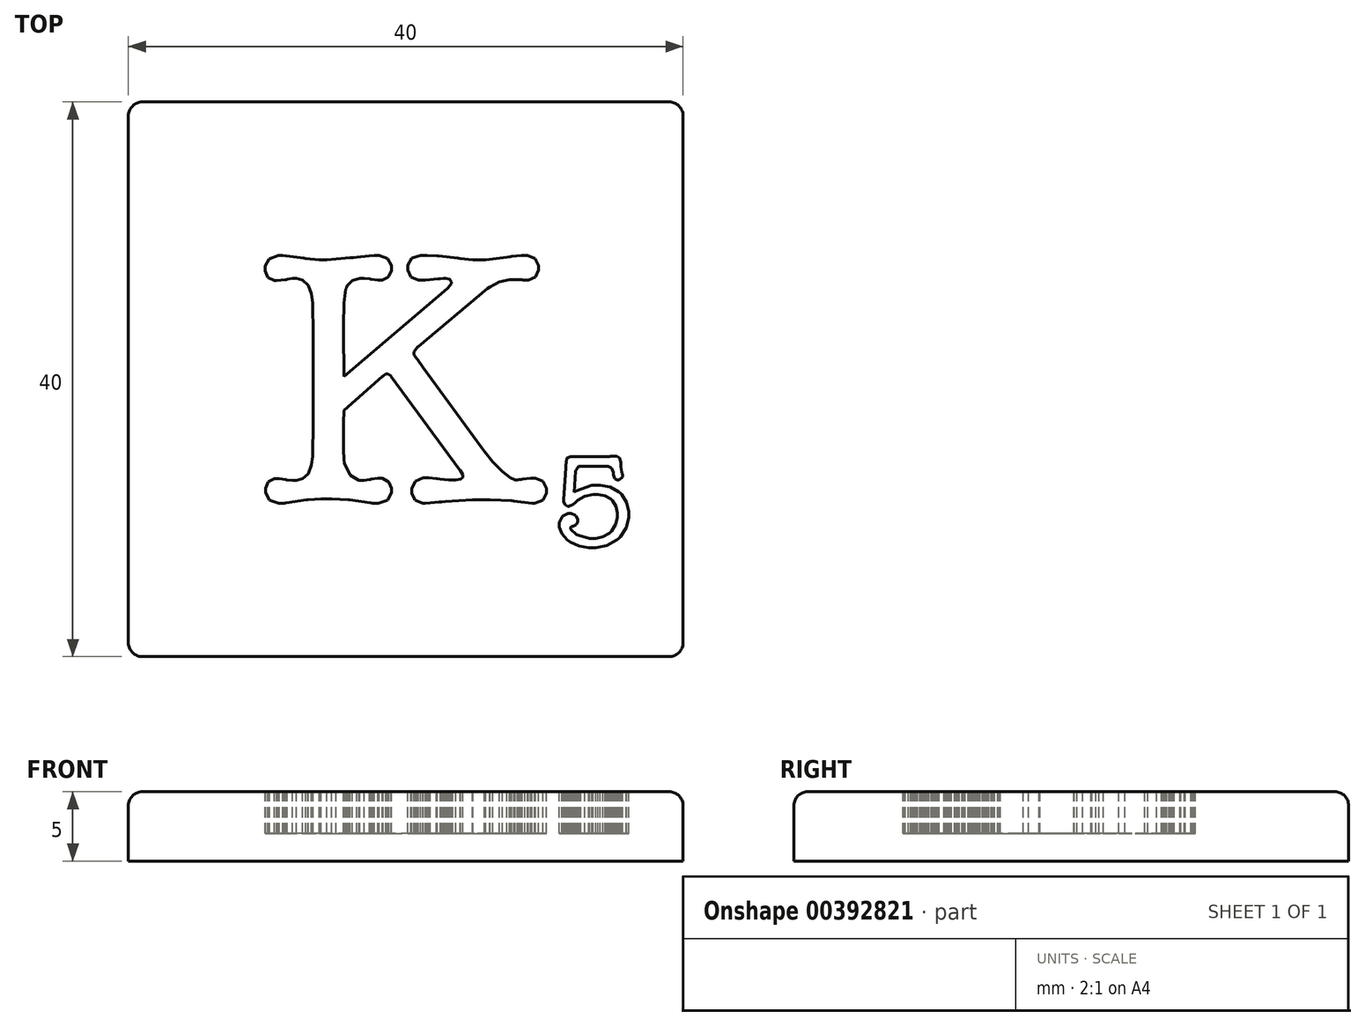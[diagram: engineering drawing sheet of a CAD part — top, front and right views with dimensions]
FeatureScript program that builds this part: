
annotation { "Feature Type Name" : "Feature", "Feature Type Description" : "" }
export const myFeature = defineFeature(function(context is Context, id is Id, definition is map)
    precondition{}
    {
        {
            var Q0;
            Q0=qCreatedBy(makeId("Top.planeOp"),FACE);
            var sketch = newSketch(context, id + "F0", { "sketchPlane" : qUnion([Q0])});
            skLineSegment(sketch, "E0.bottom", {"start": v(20, -20) * mm, "end": v(-20, -20) * mm});
            skLineSegment(sketch, "E0.top", {"start": v(20, 20) * mm, "end": v(-20, 20) * mm});
            skLineSegment(sketch, "E0.left", {"start": v(20, -20) * mm, "end": v(20, 20) * mm});
            skLineSegment(sketch, "E0.right", {"start": v(-20, -20) * mm, "end": v(-20, 20) * mm});
            skPoint(sketch, "E0.middle", {"position": v(0, 0) * mm});
            skSolve(sketch);
        }
        {
            var Q0;
            Q0=makeQuery(id+"F0.imprint","IMPRINT",FACE,{"disambiguationData":[TD([[makeQuery(id+"F0.imprint","IMPRINT",EDGE,{"derivedFrom":sQuery(id+"F0.wireOp",EDGE,"E0.bottom")}),-1.0]])]});
            extrude(context, id + "F1", {"entities" : qUnion([Q0]), "depth" : -5 * mm});
        }
        {
            var Q0;
            Q0=makeQuery(id+"F1.opExtrude","CAP_FACE",FACE,{"disambiguationData":[OSD([sQuery(id+"F0.wireOp",EDGE,"E0.bottom"),sQuery(id+"F0.wireOp",EDGE,"E0.top"),sQuery(id+"F0.wireOp",EDGE,"E0.left"),sQuery(id+"F0.wireOp",EDGE,"E0.right")])],"isStart":true});
            var Q1;
            Q1=makeQuery(id+"F1.opExtrude","SWEPT_EDGE",EDGE,{"disambiguationData":[OSD([sQuery(id+"F0.wireOp",EDGE,"E0.top"),sQuery(id+"F0.wireOp",EDGE,"E0.right")])]});
            var Q2;
            Q2=makeQuery(id+"F1.opExtrude","SWEPT_EDGE",EDGE,{"disambiguationData":[OSD([sQuery(id+"F0.wireOp",EDGE,"E0.top"),sQuery(id+"F0.wireOp",EDGE,"E0.left")])]});
            var Q3;
            Q3=makeQuery(id+"F1.opExtrude","SWEPT_EDGE",EDGE,{"disambiguationData":[OSD([sQuery(id+"F0.wireOp",EDGE,"E0.bottom"),sQuery(id+"F0.wireOp",EDGE,"E0.right")])]});
            var Q4;
            Q4=makeQuery(id+"F1.opExtrude","SWEPT_EDGE",EDGE,{"disambiguationData":[OSD([sQuery(id+"F0.wireOp",EDGE,"E0.bottom"),sQuery(id+"F0.wireOp",EDGE,"E0.left")])]});
            fillet(context, id + "F2", {"entities" : qUnion([Q0, Q1, Q2, Q3, Q4]), "radius" : 1 * mm, "tangentPropagation" : true, "allowEdgeOverflow" : false});
        }
        {
            var Q0;
            Q0=qCreatedBy(makeId("Top.planeOp"),FACE);
            var sketch = newSketch(context, id + "F3", { "sketchPlane" : qUnion([Q0])});
            skLineSegment(sketch, "E1", {"start": v(-4.46, 0.19) * mm, "end": v(3, 6.54) * mm});
            skLineSegment(sketch, "E2", {"start": v(3, 6.54) * mm, "end": v(3.05, 6.58) * mm});
            skLineSegment(sketch, "E3", {"start": v(3.05, 6.58) * mm, "end": v(3.3, 6.88) * mm});
            skLineSegment(sketch, "E4", {"start": v(3.3, 6.88) * mm, "end": v(3.3, 6.98) * mm});
            skLineSegment(sketch, "E5", {"start": v(3.3, 6.98) * mm, "end": v(3.3, 7.04) * mm});
            skLineSegment(sketch, "E6", {"start": v(3.3, 7.04) * mm, "end": v(3.17, 7.2) * mm});
            skLineSegment(sketch, "E7", {"start": v(3.17, 7.2) * mm, "end": v(2.88, 7.28) * mm});
            skLineSegment(sketch, "E8", {"start": v(2.88, 7.28) * mm, "end": v(2.8, 7.28) * mm});
            skLineSegment(sketch, "E9", {"start": v(2.8, 7.28) * mm, "end": v(2.72, 7.28) * mm});
            skLineSegment(sketch, "E10", {"start": v(2.72, 7.28) * mm, "end": v(2.51, 7.25) * mm});
            skLineSegment(sketch, "E11", {"start": v(2.51, 7.25) * mm, "end": v(2.5, 7.25) * mm});
            skLineSegment(sketch, "E12", {"start": v(2.5, 7.25) * mm, "end": v(2.34, 7.23) * mm});
            skLineSegment(sketch, "E13", {"start": v(2.34, 7.23) * mm, "end": v(1.4, 7.14) * mm});
            skLineSegment(sketch, "E14", {"start": v(1.4, 7.14) * mm, "end": v(1.1, 7.14) * mm});
            skLineSegment(sketch, "E15", {"start": v(1.1, 7.14) * mm, "end": v(0.92, 7.14) * mm});
            skLineSegment(sketch, "E16", {"start": v(0.92, 7.14) * mm, "end": v(0.38, 7.38) * mm});
            skLineSegment(sketch, "E17", {"start": v(0.38, 7.38) * mm, "end": v(0.14, 7.9) * mm});
            skLineSegment(sketch, "E18", {"start": v(0.14, 7.9) * mm, "end": v(0.14, 8.07) * mm});
            skLineSegment(sketch, "E19", {"start": v(0.14, 8.07) * mm, "end": v(0.14, 8.23) * mm});
            skLineSegment(sketch, "E20", {"start": v(0.14, 8.23) * mm, "end": v(0.43, 8.73) * mm});
            skLineSegment(sketch, "E21", {"start": v(0.43, 8.73) * mm, "end": v(1.07, 8.94) * mm});
            skLineSegment(sketch, "E22", {"start": v(1.07, 8.94) * mm, "end": v(1.28, 8.94) * mm});
            skLineSegment(sketch, "E23", {"start": v(1.28, 8.94) * mm, "end": v(1.55, 8.94) * mm});
            skLineSegment(sketch, "E24", {"start": v(1.55, 8.94) * mm, "end": v(2.29, 8.9) * mm});
            skLineSegment(sketch, "E25", {"start": v(2.29, 8.9) * mm, "end": v(2.37, 8.9) * mm});
            skLineSegment(sketch, "E26", {"start": v(2.37, 8.9) * mm, "end": v(3.77, 8.73) * mm});
            skLineSegment(sketch, "E27", {"start": v(3.77, 8.73) * mm, "end": v(3.92, 8.71) * mm});
            skLineSegment(sketch, "E28", {"start": v(3.92, 8.71) * mm, "end": v(4.86, 8.63) * mm});
            skLineSegment(sketch, "E29", {"start": v(4.86, 8.63) * mm, "end": v(5.17, 8.63) * mm});
            skLineSegment(sketch, "E30", {"start": v(5.17, 8.63) * mm, "end": v(5.76, 8.63) * mm});
            skLineSegment(sketch, "E31", {"start": v(5.76, 8.63) * mm, "end": v(7.3, 8.8) * mm});
            skLineSegment(sketch, "E32", {"start": v(7.3, 8.8) * mm, "end": v(7.53, 8.84) * mm});
            skLineSegment(sketch, "E33", {"start": v(7.53, 8.84) * mm, "end": v(7.65, 8.85) * mm});
            skLineSegment(sketch, "E34", {"start": v(7.65, 8.85) * mm, "end": v(8.35, 8.94) * mm});
            skLineSegment(sketch, "E35", {"start": v(8.35, 8.94) * mm, "end": v(8.59, 8.94) * mm});
            skLineSegment(sketch, "E36", {"start": v(8.59, 8.94) * mm, "end": v(8.77, 8.94) * mm});
            skLineSegment(sketch, "E37", {"start": v(8.77, 8.94) * mm, "end": v(9.34, 8.72) * mm});
            skLineSegment(sketch, "E38", {"start": v(9.34, 8.72) * mm, "end": v(9.6, 8.21) * mm});
            skLineSegment(sketch, "E39", {"start": v(9.6, 8.21) * mm, "end": v(9.6, 8.04) * mm});
            skLineSegment(sketch, "E40", {"start": v(9.6, 8.04) * mm, "end": v(9.6, 7.87) * mm});
            skLineSegment(sketch, "E41", {"start": v(9.6, 7.87) * mm, "end": v(9.36, 7.37) * mm});
            skLineSegment(sketch, "E42", {"start": v(9.36, 7.37) * mm, "end": v(8.84, 7.14) * mm});
            skLineSegment(sketch, "E43", {"start": v(8.84, 7.14) * mm, "end": v(8.67, 7.14) * mm});
            skLineSegment(sketch, "E44", {"start": v(8.67, 7.14) * mm, "end": v(8.6, 7.14) * mm});
            skLineSegment(sketch, "E45", {"start": v(8.6, 7.14) * mm, "end": v(8.43, 7.17) * mm});
            skLineSegment(sketch, "E46", {"start": v(8.43, 7.17) * mm, "end": v(8.4, 7.17) * mm});
            skLineSegment(sketch, "E47", {"start": v(8.4, 7.17) * mm, "end": v(8.1, 7.17) * mm});
            skLineSegment(sketch, "E48", {"start": v(8.1, 7.17) * mm, "end": v(8.09, 7.18) * mm});
            skLineSegment(sketch, "E49", {"start": v(8.09, 7.18) * mm, "end": v(7.8, 7.2) * mm});
            skLineSegment(sketch, "E50", {"start": v(7.8, 7.2) * mm, "end": v(7.71, 7.2) * mm});
            skLineSegment(sketch, "E51", {"start": v(7.71, 7.2) * mm, "end": v(7.47, 7.2) * mm});
            skLineSegment(sketch, "E52", {"start": v(7.47, 7.2) * mm, "end": v(6.76, 7.03) * mm});
            skLineSegment(sketch, "E53", {"start": v(6.76, 7.03) * mm, "end": v(6.05, 6.65) * mm});
            skLineSegment(sketch, "E54", {"start": v(6.05, 6.65) * mm, "end": v(5.91, 6.54) * mm});
            skLineSegment(sketch, "E55", {"start": v(5.91, 6.54) * mm, "end": v(0.91, 2.35) * mm});
            skLineSegment(sketch, "E56", {"start": v(0.91, 2.35) * mm, "end": v(0.86, 2.31) * mm});
            skLineSegment(sketch, "E57", {"start": v(0.86, 2.31) * mm, "end": v(0.6, 1.99) * mm});
            skLineSegment(sketch, "E58", {"start": v(0.6, 1.99) * mm, "end": v(0.6, 1.88) * mm});
            skLineSegment(sketch, "E59", {"start": v(0.6, 1.88) * mm, "end": v(0.6, 1.77) * mm});
            skLineSegment(sketch, "E60", {"start": v(0.6, 1.77) * mm, "end": v(0.82, 1.48) * mm});
            skLineSegment(sketch, "E61", {"start": v(0.82, 1.48) * mm, "end": v(0.86, 1.43) * mm});
            skLineSegment(sketch, "E62", {"start": v(0.86, 1.43) * mm, "end": v(1.26, 0.82) * mm});
            skLineSegment(sketch, "E63", {"start": v(1.26, 0.82) * mm, "end": v(5.5, -4.95) * mm});
            skLineSegment(sketch, "E64", {"start": v(5.5, -4.95) * mm, "end": v(5.68, -5.2) * mm});
            skLineSegment(sketch, "E65", {"start": v(5.68, -5.2) * mm, "end": v(6.28, -5.95) * mm});
            skLineSegment(sketch, "E66", {"start": v(6.28, -5.95) * mm, "end": v(6.97, -6.67) * mm});
            skLineSegment(sketch, "E67", {"start": v(6.97, -6.67) * mm, "end": v(7.55, -7.1) * mm});
            skLineSegment(sketch, "E68", {"start": v(7.55, -7.1) * mm, "end": v(7.9, -7.25) * mm});
            skLineSegment(sketch, "E69", {"start": v(7.9, -7.25) * mm, "end": v(8.03, -7.25) * mm});
            skLineSegment(sketch, "E70", {"start": v(8.03, -7.25) * mm, "end": v(8.07, -7.25) * mm});
            skLineSegment(sketch, "E71", {"start": v(8.07, -7.25) * mm, "end": v(8.17, -7.23) * mm});
            skLineSegment(sketch, "E72", {"start": v(8.17, -7.23) * mm, "end": v(8.19, -7.22) * mm});
            skLineSegment(sketch, "E73", {"start": v(8.19, -7.22) * mm, "end": v(8.32, -7.22) * mm});
            skLineSegment(sketch, "E74", {"start": v(8.32, -7.22) * mm, "end": v(8.44, -7.2) * mm});
            skLineSegment(sketch, "E75", {"start": v(8.44, -7.2) * mm, "end": v(9, -7.14) * mm});
            skLineSegment(sketch, "E76", {"start": v(9, -7.14) * mm, "end": v(9.2, -7.14) * mm});
            skLineSegment(sketch, "E77", {"start": v(9.2, -7.14) * mm, "end": v(9.37, -7.14) * mm});
            skLineSegment(sketch, "E78", {"start": v(9.37, -7.14) * mm, "end": v(9.9, -7.37) * mm});
            skLineSegment(sketch, "E79", {"start": v(9.9, -7.37) * mm, "end": v(10.15, -7.87) * mm});
            skLineSegment(sketch, "E80", {"start": v(10.15, -7.87) * mm, "end": v(10.15, -8.04) * mm});
            skLineSegment(sketch, "E81", {"start": v(10.15, -8.04) * mm, "end": v(10.15, -8.21) * mm});
            skLineSegment(sketch, "E82", {"start": v(10.15, -8.21) * mm, "end": v(9.89, -8.72) * mm});
            skLineSegment(sketch, "E83", {"start": v(9.89, -8.72) * mm, "end": v(9.3, -8.94) * mm});
            skLineSegment(sketch, "E84", {"start": v(9.3, -8.94) * mm, "end": v(9.11, -8.94) * mm});
            skLineSegment(sketch, "E85", {"start": v(9.11, -8.94) * mm, "end": v(7.8, -8.78) * mm});
            skLineSegment(sketch, "E86", {"start": v(7.8, -8.78) * mm, "end": v(7.63, -8.77) * mm});
            skLineSegment(sketch, "E87", {"start": v(7.63, -8.77) * mm, "end": v(6.08, -8.68) * mm});
            skLineSegment(sketch, "E88", {"start": v(6.08, -8.68) * mm, "end": v(5.57, -8.68) * mm});
            skLineSegment(sketch, "E89", {"start": v(5.57, -8.68) * mm, "end": v(4.82, -8.68) * mm});
            skLineSegment(sketch, "E90", {"start": v(4.82, -8.68) * mm, "end": v(2.84, -8.8) * mm});
            skLineSegment(sketch, "E91", {"start": v(2.84, -8.8) * mm, "end": v(2.58, -8.84) * mm});
            skLineSegment(sketch, "E92", {"start": v(2.58, -8.84) * mm, "end": v(2.4, -8.85) * mm});
            skLineSegment(sketch, "E93", {"start": v(2.4, -8.85) * mm, "end": v(1.77, -8.92) * mm});
            skLineSegment(sketch, "E94", {"start": v(1.77, -8.92) * mm, "end": v(1.42, -8.94) * mm});
            skLineSegment(sketch, "E95", {"start": v(1.42, -8.94) * mm, "end": v(1.23, -8.94) * mm});
            skLineSegment(sketch, "E96", {"start": v(1.23, -8.94) * mm, "end": v(0.68, -8.72) * mm});
            skLineSegment(sketch, "E97", {"start": v(0.68, -8.72) * mm, "end": v(0.44, -8.23) * mm});
            skLineSegment(sketch, "E98", {"start": v(0.44, -8.23) * mm, "end": v(0.44, -8.07) * mm});
            skLineSegment(sketch, "E99", {"start": v(0.44, -8.07) * mm, "end": v(0.44, -7.89) * mm});
            skLineSegment(sketch, "E100", {"start": v(0.44, -7.89) * mm, "end": v(0.7, -7.36) * mm});
            skLineSegment(sketch, "E101", {"start": v(0.7, -7.36) * mm, "end": v(1.27, -7.12) * mm});
            skLineSegment(sketch, "E102", {"start": v(1.27, -7.12) * mm, "end": v(1.47, -7.12) * mm});
            skLineSegment(sketch, "E103", {"start": v(1.47, -7.12) * mm, "end": v(1.67, -7.12) * mm});
            skLineSegment(sketch, "E104", {"start": v(1.67, -7.12) * mm, "end": v(2.2, -7.16) * mm});
            skLineSegment(sketch, "E105", {"start": v(2.2, -7.16) * mm, "end": v(2.29, -7.17) * mm});
            skLineSegment(sketch, "E106", {"start": v(2.29, -7.17) * mm, "end": v(2.46, -7.19) * mm});
            skLineSegment(sketch, "E107", {"start": v(2.46, -7.19) * mm, "end": v(3.1, -7.25) * mm});
            skLineSegment(sketch, "E108", {"start": v(3.1, -7.25) * mm, "end": v(3.38, -7.28) * mm});
            skLineSegment(sketch, "E109", {"start": v(3.38, -7.28) * mm, "end": v(3.48, -7.28) * mm});
            skLineSegment(sketch, "E110", {"start": v(3.48, -7.28) * mm, "end": v(3.6, -7.28) * mm});
            skLineSegment(sketch, "E111", {"start": v(3.6, -7.28) * mm, "end": v(3.95, -7.2) * mm});
            skLineSegment(sketch, "E112", {"start": v(3.95, -7.2) * mm, "end": v(4.11, -7.06) * mm});
            skLineSegment(sketch, "E113", {"start": v(4.11, -7.06) * mm, "end": v(4.11, -7.01) * mm});
            skLineSegment(sketch, "E114", {"start": v(4.11, -7.01) * mm, "end": v(4.11, -6.89) * mm});
            skLineSegment(sketch, "E115", {"start": v(4.11, -6.89) * mm, "end": v(3.91, -6.56) * mm});
            skLineSegment(sketch, "E116", {"start": v(3.91, -6.56) * mm, "end": v(3.88, -6.5) * mm});
            skLineSegment(sketch, "E117", {"start": v(3.88, -6.5) * mm, "end": v(-1.05, 0.19) * mm});
            skLineSegment(sketch, "E118", {"start": v(-1.05, 0.19) * mm, "end": v(-1.07, 0.22) * mm});
            skLineSegment(sketch, "E119", {"start": v(-1.07, 0.22) * mm, "end": v(-1.27, 0.4) * mm});
            skLineSegment(sketch, "E120", {"start": v(-1.27, 0.4) * mm, "end": v(-1.34, 0.4) * mm});
            skLineSegment(sketch, "E121", {"start": v(-1.34, 0.4) * mm, "end": v(-1.42, 0.4) * mm});
            skLineSegment(sketch, "E122", {"start": v(-1.42, 0.4) * mm, "end": v(-1.64, 0.22) * mm});
            skLineSegment(sketch, "E123", {"start": v(-1.64, 0.22) * mm, "end": v(-1.68, 0.19) * mm});
            skLineSegment(sketch, "E124", {"start": v(-1.68, 0.19) * mm, "end": v(-4.46, -2.25) * mm});
            skLineSegment(sketch, "E125", {"start": v(-4.46, -2.25) * mm, "end": v(-4.46, -2.33) * mm});
            skLineSegment(sketch, "E126", {"start": v(-4.46, -2.33) * mm, "end": v(-4.49, -3.08) * mm});
            skLineSegment(sketch, "E127", {"start": v(-4.49, -3.08) * mm, "end": v(-4.49, -3.33) * mm});
            skLineSegment(sketch, "E128", {"start": v(-4.49, -3.33) * mm, "end": v(-4.49, -3.78) * mm});
            skLineSegment(sketch, "E129", {"start": v(-4.49, -3.78) * mm, "end": v(-4.48, -5.1) * mm});
            skLineSegment(sketch, "E130", {"start": v(-4.48, -5.1) * mm, "end": v(-4.46, -5.77) * mm});
            skLineSegment(sketch, "E131", {"start": v(-4.46, -5.77) * mm, "end": v(-4.46, -5.8) * mm});
            skLineSegment(sketch, "E132", {"start": v(-4.46, -5.8) * mm, "end": v(-4.42, -6.04) * mm});
            skLineSegment(sketch, "E133", {"start": v(-4.42, -6.04) * mm, "end": v(-4.02, -6.93) * mm});
            skLineSegment(sketch, "E134", {"start": v(-4.02, -6.93) * mm, "end": v(-3.36, -7.3) * mm});
            skLineSegment(sketch, "E135", {"start": v(-3.36, -7.3) * mm, "end": v(-3.14, -7.3) * mm});
            skLineSegment(sketch, "E136", {"start": v(-3.14, -7.3) * mm, "end": v(-3, -7.3) * mm});
            skLineSegment(sketch, "E137", {"start": v(-3, -7.3) * mm, "end": v(-2.63, -7.24) * mm});
            skLineSegment(sketch, "E138", {"start": v(-2.63, -7.24) * mm, "end": v(-2.55, -7.22) * mm});
            skLineSegment(sketch, "E139", {"start": v(-2.55, -7.22) * mm, "end": v(-2.48, -7.2) * mm});
            skLineSegment(sketch, "E140", {"start": v(-2.48, -7.2) * mm, "end": v(-2, -7.14) * mm});
            skLineSegment(sketch, "E141", {"start": v(-2, -7.14) * mm, "end": v(-1.84, -7.14) * mm});
            skLineSegment(sketch, "E142", {"start": v(-1.84, -7.14) * mm, "end": v(-1.7, -7.14) * mm});
            skLineSegment(sketch, "E143", {"start": v(-1.7, -7.14) * mm, "end": v(-1.3, -7.35) * mm});
            skLineSegment(sketch, "E144", {"start": v(-1.3, -7.35) * mm, "end": v(-1.26, -7.4) * mm});
            skLineSegment(sketch, "E145", {"start": v(-1.26, -7.4) * mm, "end": v(-1.22, -7.44) * mm});
            skLineSegment(sketch, "E146", {"start": v(-1.22, -7.44) * mm, "end": v(-1.02, -7.87) * mm});
            skLineSegment(sketch, "E147", {"start": v(-1.02, -7.87) * mm, "end": v(-1.02, -8.02) * mm});
            skLineSegment(sketch, "E148", {"start": v(-1.02, -8.02) * mm, "end": v(-1.02, -8.2) * mm});
            skLineSegment(sketch, "E149", {"start": v(-1.02, -8.2) * mm, "end": v(-1.31, -8.71) * mm});
            skLineSegment(sketch, "E150", {"start": v(-1.31, -8.71) * mm, "end": v(-1.97, -8.94) * mm});
            skLineSegment(sketch, "E151", {"start": v(-1.97, -8.94) * mm, "end": v(-2.18, -8.94) * mm});
            skLineSegment(sketch, "E152", {"start": v(-2.18, -8.94) * mm, "end": v(-2.37, -8.94) * mm});
            skLineSegment(sketch, "E153", {"start": v(-2.37, -8.94) * mm, "end": v(-2.39, -8.94) * mm});
            skLineSegment(sketch, "E154", {"start": v(-2.39, -8.94) * mm, "end": v(-2.51, -8.92) * mm});
            skLineSegment(sketch, "E155", {"start": v(-2.51, -8.92) * mm, "end": v(-2.55, -8.92) * mm});
            skLineSegment(sketch, "E156", {"start": v(-2.55, -8.92) * mm, "end": v(-4.03, -8.7) * mm});
            skLineSegment(sketch, "E157", {"start": v(-4.03, -8.7) * mm, "end": v(-4.13, -8.7) * mm});
            skLineSegment(sketch, "E158", {"start": v(-4.13, -8.7) * mm, "end": v(-5.35, -8.63) * mm});
            skLineSegment(sketch, "E159", {"start": v(-5.35, -8.63) * mm, "end": v(-5.75, -8.63) * mm});
            skLineSegment(sketch, "E160", {"start": v(-5.75, -8.63) * mm, "end": v(-6.1, -8.63) * mm});
            skLineSegment(sketch, "E161", {"start": v(-6.1, -8.63) * mm, "end": v(-7.07, -8.7) * mm});
            skLineSegment(sketch, "E162", {"start": v(-7.07, -8.7) * mm, "end": v(-7.16, -8.7) * mm});
            skLineSegment(sketch, "E163", {"start": v(-7.16, -8.7) * mm, "end": v(-8.61, -8.92) * mm});
            skLineSegment(sketch, "E164", {"start": v(-8.61, -8.92) * mm, "end": v(-8.65, -8.92) * mm});
            skLineSegment(sketch, "E165", {"start": v(-8.65, -8.92) * mm, "end": v(-8.75, -8.94) * mm});
            skLineSegment(sketch, "E166", {"start": v(-8.75, -8.94) * mm, "end": v(-8.77, -8.94) * mm});
            skLineSegment(sketch, "E167", {"start": v(-8.77, -8.94) * mm, "end": v(-8.93, -8.94) * mm});
            skLineSegment(sketch, "E168", {"start": v(-8.93, -8.94) * mm, "end": v(-9.15, -8.94) * mm});
            skLineSegment(sketch, "E169", {"start": v(-9.15, -8.94) * mm, "end": v(-9.82, -8.71) * mm});
            skLineSegment(sketch, "E170", {"start": v(-9.82, -8.71) * mm, "end": v(-10.12, -8.2) * mm});
            skLineSegment(sketch, "E171", {"start": v(-10.12, -8.2) * mm, "end": v(-10.12, -8.02) * mm});
            skLineSegment(sketch, "E172", {"start": v(-10.12, -8.02) * mm, "end": v(-10.12, -7.86) * mm});
            skLineSegment(sketch, "E173", {"start": v(-10.12, -7.86) * mm, "end": v(-9.92, -7.38) * mm});
            skLineSegment(sketch, "E174", {"start": v(-9.92, -7.38) * mm, "end": v(-9.45, -7.17) * mm});
            skLineSegment(sketch, "E175", {"start": v(-9.45, -7.17) * mm, "end": v(-9.3, -7.17) * mm});
            skLineSegment(sketch, "E176", {"start": v(-9.3, -7.17) * mm, "end": v(-9.12, -7.17) * mm});
            skLineSegment(sketch, "E177", {"start": v(-9.12, -7.17) * mm, "end": v(-8.67, -7.24) * mm});
            skLineSegment(sketch, "E178", {"start": v(-8.67, -7.24) * mm, "end": v(-8.59, -7.25) * mm});
            skLineSegment(sketch, "E179", {"start": v(-8.59, -7.25) * mm, "end": v(-8.53, -7.26) * mm});
            skLineSegment(sketch, "E180", {"start": v(-8.53, -7.26) * mm, "end": v(-8.16, -7.3) * mm});
            skLineSegment(sketch, "E181", {"start": v(-8.16, -7.3) * mm, "end": v(-8.03, -7.3) * mm});
            skLineSegment(sketch, "E182", {"start": v(-8.03, -7.3) * mm, "end": v(-7.89, -7.3) * mm});
            skLineSegment(sketch, "E183", {"start": v(-7.89, -7.3) * mm, "end": v(-7.45, -7.18) * mm});
            skLineSegment(sketch, "E184", {"start": v(-7.45, -7.18) * mm, "end": v(-7.04, -6.8) * mm});
            skLineSegment(sketch, "E185", {"start": v(-7.04, -6.8) * mm, "end": v(-6.79, -6.19) * mm});
            skLineSegment(sketch, "E186", {"start": v(-6.79, -6.19) * mm, "end": v(-6.7, -5.53) * mm});
            skLineSegment(sketch, "E187", {"start": v(-6.7, -5.53) * mm, "end": v(-6.7, -5.32) * mm});
            skLineSegment(sketch, "E188", {"start": v(-6.7, -5.32) * mm, "end": v(-6.7, -4.88) * mm});
            skLineSegment(sketch, "E189", {"start": v(-6.7, -4.88) * mm, "end": v(-6.69, -3.78) * mm});
            skLineSegment(sketch, "E190", {"start": v(-6.69, -3.78) * mm, "end": v(-6.68, -3.47) * mm});
            skLineSegment(sketch, "E191", {"start": v(-6.68, -3.47) * mm, "end": v(-6.68, 3.44) * mm});
            skLineSegment(sketch, "E192", {"start": v(-6.68, 3.44) * mm, "end": v(-6.7, 5.3) * mm});
            skLineSegment(sketch, "E193", {"start": v(-6.7, 5.3) * mm, "end": v(-6.7, 5.51) * mm});
            skLineSegment(sketch, "E194", {"start": v(-6.7, 5.51) * mm, "end": v(-6.79, 6.16) * mm});
            skLineSegment(sketch, "E195", {"start": v(-6.79, 6.16) * mm, "end": v(-7.04, 6.78) * mm});
            skLineSegment(sketch, "E196", {"start": v(-7.04, 6.78) * mm, "end": v(-7.45, 7.15) * mm});
            skLineSegment(sketch, "E197", {"start": v(-7.45, 7.15) * mm, "end": v(-7.89, 7.28) * mm});
            skLineSegment(sketch, "E198", {"start": v(-7.89, 7.28) * mm, "end": v(-8.03, 7.28) * mm});
            skLineSegment(sketch, "E199", {"start": v(-8.03, 7.28) * mm, "end": v(-8.17, 7.28) * mm});
            skLineSegment(sketch, "E200", {"start": v(-8.17, 7.28) * mm, "end": v(-8.54, 7.21) * mm});
            skLineSegment(sketch, "E201", {"start": v(-8.54, 7.21) * mm, "end": v(-8.59, 7.2) * mm});
            skLineSegment(sketch, "E202", {"start": v(-8.59, 7.2) * mm, "end": v(-8.67, 7.18) * mm});
            skLineSegment(sketch, "E203", {"start": v(-8.67, 7.18) * mm, "end": v(-9.3, 7.12) * mm});
            skLineSegment(sketch, "E204", {"start": v(-9.3, 7.12) * mm, "end": v(-9.46, 7.12) * mm});
            skLineSegment(sketch, "E205", {"start": v(-9.46, 7.12) * mm, "end": v(-9.94, 7.34) * mm});
            skLineSegment(sketch, "E206", {"start": v(-9.94, 7.34) * mm, "end": v(-10.15, 7.83) * mm});
            skLineSegment(sketch, "E207", {"start": v(-10.15, 7.83) * mm, "end": v(-10.15, 8) * mm});
            skLineSegment(sketch, "E208", {"start": v(-10.15, 8) * mm, "end": v(-10.15, 8.16) * mm});
            skLineSegment(sketch, "E209", {"start": v(-10.15, 8.16) * mm, "end": v(-9.85, 8.69) * mm});
            skLineSegment(sketch, "E210", {"start": v(-9.85, 8.69) * mm, "end": v(-9.18, 8.92) * mm});
            skLineSegment(sketch, "E211", {"start": v(-9.18, 8.92) * mm, "end": v(-8.96, 8.92) * mm});
            skLineSegment(sketch, "E212", {"start": v(-8.96, 8.92) * mm, "end": v(-8.87, 8.92) * mm});
            skLineSegment(sketch, "E213", {"start": v(-8.87, 8.92) * mm, "end": v(-8.65, 8.9) * mm});
            skLineSegment(sketch, "E214", {"start": v(-8.65, 8.9) * mm, "end": v(-8.61, 8.9) * mm});
            skLineSegment(sketch, "E215", {"start": v(-8.61, 8.9) * mm, "end": v(-7.34, 8.73) * mm});
            skLineSegment(sketch, "E216", {"start": v(-7.34, 8.73) * mm, "end": v(-7.2, 8.71) * mm});
            skLineSegment(sketch, "E217", {"start": v(-7.2, 8.71) * mm, "end": v(-6.24, 8.63) * mm});
            skLineSegment(sketch, "E218", {"start": v(-6.24, 8.63) * mm, "end": v(-5.91, 8.63) * mm});
            skLineSegment(sketch, "E219", {"start": v(-5.91, 8.63) * mm, "end": v(-5.7, 8.63) * mm});
            skLineSegment(sketch, "E220", {"start": v(-5.7, 8.63) * mm, "end": v(-5.02, 8.67) * mm});
            skLineSegment(sketch, "E221", {"start": v(-5.02, 8.67) * mm, "end": v(-4, 8.76) * mm});
            skLineSegment(sketch, "E222", {"start": v(-4, 8.76) * mm, "end": v(-3.77, 8.78) * mm});
            skLineSegment(sketch, "E223", {"start": v(-3.77, 8.78) * mm, "end": v(-3.53, 8.81) * mm});
            skLineSegment(sketch, "E224", {"start": v(-3.53, 8.81) * mm, "end": v(-2.65, 8.9) * mm});
            skLineSegment(sketch, "E225", {"start": v(-2.65, 8.9) * mm, "end": v(-2.26, 8.94) * mm});
            skLineSegment(sketch, "E226", {"start": v(-2.26, 8.94) * mm, "end": v(-2.13, 8.94) * mm});
            skLineSegment(sketch, "E227", {"start": v(-2.13, 8.94) * mm, "end": v(-1.92, 8.94) * mm});
            skLineSegment(sketch, "E228", {"start": v(-1.92, 8.94) * mm, "end": v(-1.3, 8.71) * mm});
            skLineSegment(sketch, "E229", {"start": v(-1.3, 8.71) * mm, "end": v(-1.02, 8.2) * mm});
            skLineSegment(sketch, "E230", {"start": v(-1.02, 8.2) * mm, "end": v(-1.02, 8.02) * mm});
            skLineSegment(sketch, "E231", {"start": v(-1.02, 8.02) * mm, "end": v(-1.02, 7.86) * mm});
            skLineSegment(sketch, "E232", {"start": v(-1.02, 7.86) * mm, "end": v(-1.22, 7.44) * mm});
            skLineSegment(sketch, "E233", {"start": v(-1.22, 7.44) * mm, "end": v(-1.26, 7.4) * mm});
            skLineSegment(sketch, "E234", {"start": v(-1.26, 7.4) * mm, "end": v(-1.3, 7.35) * mm});
            skLineSegment(sketch, "E235", {"start": v(-1.3, 7.35) * mm, "end": v(-1.7, 7.14) * mm});
            skLineSegment(sketch, "E236", {"start": v(-1.7, 7.14) * mm, "end": v(-1.84, 7.14) * mm});
            skLineSegment(sketch, "E237", {"start": v(-1.84, 7.14) * mm, "end": v(-2.02, 7.14) * mm});
            skLineSegment(sketch, "E238", {"start": v(-2.02, 7.14) * mm, "end": v(-2.48, 7.21) * mm});
            skLineSegment(sketch, "E239", {"start": v(-2.48, 7.21) * mm, "end": v(-2.55, 7.22) * mm});
            skLineSegment(sketch, "E240", {"start": v(-2.55, 7.22) * mm, "end": v(-2.59, 7.23) * mm});
            skLineSegment(sketch, "E241", {"start": v(-2.59, 7.23) * mm, "end": v(-2.98, 7.28) * mm});
            skLineSegment(sketch, "E242", {"start": v(-2.98, 7.28) * mm, "end": v(-3.1, 7.28) * mm});
            skLineSegment(sketch, "E243", {"start": v(-3.1, 7.28) * mm, "end": v(-3.3, 7.28) * mm});
            skLineSegment(sketch, "E244", {"start": v(-3.3, 7.28) * mm, "end": v(-3.86, 7.12) * mm});
            skLineSegment(sketch, "E245", {"start": v(-3.86, 7.12) * mm, "end": v(-4.23, 6.74) * mm});
            skLineSegment(sketch, "E246", {"start": v(-4.23, 6.74) * mm, "end": v(-4.27, 6.63) * mm});
            skLineSegment(sketch, "E247", {"start": v(-4.27, 6.63) * mm, "end": v(-4.31, 6.52) * mm});
            skLineSegment(sketch, "E248", {"start": v(-4.31, 6.52) * mm, "end": v(-4.45, 5.51) * mm});
            skLineSegment(sketch, "E249", {"start": v(-4.45, 5.51) * mm, "end": v(-4.49, 3.89) * mm});
            skLineSegment(sketch, "E250", {"start": v(-4.49, 3.89) * mm, "end": v(-4.49, 3.47) * mm});
            skLineSegment(sketch, "E251", {"start": v(-4.49, 3.47) * mm, "end": v(-4.46, 0.19) * mm});
            skSolve(sketch);
        }
        {
            var Q0;
            Q0=qCreatedBy(makeId("Top.planeOp"),FACE);
            var sketch = newSketch(context, id + "F4", { "sketchPlane" : qUnion([Q0])});
            skLineSegment(sketch, "E252", {"start": v(12.26, -6.63) * mm, "end": v(12.15, -8.15) * mm});
            skLineSegment(sketch, "E253", {"start": v(12.15, -8.15) * mm, "end": v(12.27, -8.07) * mm});
            skLineSegment(sketch, "E254", {"start": v(12.27, -8.07) * mm, "end": v(13.4, -7.64) * mm});
            skLineSegment(sketch, "E255", {"start": v(13.4, -7.64) * mm, "end": v(13.79, -7.64) * mm});
            skLineSegment(sketch, "E256", {"start": v(13.79, -7.64) * mm, "end": v(14.02, -7.64) * mm});
            skLineSegment(sketch, "E257", {"start": v(14.02, -7.64) * mm, "end": v(14.74, -7.78) * mm});
            skLineSegment(sketch, "E258", {"start": v(14.74, -7.78) * mm, "end": v(15.37, -8.11) * mm});
            skLineSegment(sketch, "E259", {"start": v(15.37, -8.11) * mm, "end": v(15.47, -8.2) * mm});
            skLineSegment(sketch, "E260", {"start": v(15.47, -8.2) * mm, "end": v(15.57, -8.3) * mm});
            skLineSegment(sketch, "E261", {"start": v(15.57, -8.3) * mm, "end": v(15.93, -8.88) * mm});
            skLineSegment(sketch, "E262", {"start": v(15.93, -8.88) * mm, "end": v(16.09, -9.53) * mm});
            skLineSegment(sketch, "E263", {"start": v(16.09, -9.53) * mm, "end": v(16.09, -9.75) * mm});
            skLineSegment(sketch, "E264", {"start": v(16.09, -9.75) * mm, "end": v(16.09, -10) * mm});
            skLineSegment(sketch, "E265", {"start": v(16.09, -10) * mm, "end": v(15.9, -10.72) * mm});
            skLineSegment(sketch, "E266", {"start": v(15.9, -10.72) * mm, "end": v(15.48, -11.37) * mm});
            skLineSegment(sketch, "E267", {"start": v(15.48, -11.37) * mm, "end": v(15.35, -11.48) * mm});
            skLineSegment(sketch, "E268", {"start": v(15.35, -11.48) * mm, "end": v(15.23, -11.6) * mm});
            skLineSegment(sketch, "E269", {"start": v(15.23, -11.6) * mm, "end": v(14.5, -11.98) * mm});
            skLineSegment(sketch, "E270", {"start": v(14.5, -11.98) * mm, "end": v(13.7, -12.14) * mm});
            skLineSegment(sketch, "E271", {"start": v(13.7, -12.14) * mm, "end": v(13.42, -12.14) * mm});
            skLineSegment(sketch, "E272", {"start": v(13.42, -12.14) * mm, "end": v(13.2, -12.14) * mm});
            skLineSegment(sketch, "E273", {"start": v(13.2, -12.14) * mm, "end": v(12.52, -12.02) * mm});
            skLineSegment(sketch, "E274", {"start": v(12.52, -12.02) * mm, "end": v(11.87, -11.74) * mm});
            skLineSegment(sketch, "E275", {"start": v(11.87, -11.74) * mm, "end": v(11.76, -11.66) * mm});
            skLineSegment(sketch, "E276", {"start": v(11.76, -11.66) * mm, "end": v(11.65, -11.58) * mm});
            skLineSegment(sketch, "E277", {"start": v(11.65, -11.58) * mm, "end": v(11.25, -11.13) * mm});
            skLineSegment(sketch, "E278", {"start": v(11.25, -11.13) * mm, "end": v(11.08, -10.65) * mm});
            skLineSegment(sketch, "E279", {"start": v(11.08, -10.65) * mm, "end": v(11.08, -10.49) * mm});
            skLineSegment(sketch, "E280", {"start": v(11.08, -10.49) * mm, "end": v(11.08, -10.34) * mm});
            skLineSegment(sketch, "E281", {"start": v(11.08, -10.34) * mm, "end": v(11.26, -9.95) * mm});
            skLineSegment(sketch, "E282", {"start": v(11.26, -9.95) * mm, "end": v(11.3, -9.91) * mm});
            skLineSegment(sketch, "E283", {"start": v(11.3, -9.91) * mm, "end": v(11.34, -9.87) * mm});
            skLineSegment(sketch, "E284", {"start": v(11.34, -9.87) * mm, "end": v(11.7, -9.68) * mm});
            skLineSegment(sketch, "E285", {"start": v(11.7, -9.68) * mm, "end": v(11.83, -9.68) * mm});
            skLineSegment(sketch, "E286", {"start": v(11.83, -9.68) * mm, "end": v(11.93, -9.68) * mm});
            skLineSegment(sketch, "E287", {"start": v(11.93, -9.68) * mm, "end": v(12.21, -9.8) * mm});
            skLineSegment(sketch, "E288", {"start": v(12.21, -9.8) * mm, "end": v(12.24, -9.82) * mm});
            skLineSegment(sketch, "E289", {"start": v(12.24, -9.82) * mm, "end": v(12.26, -9.84) * mm});
            skLineSegment(sketch, "E290", {"start": v(12.26, -9.84) * mm, "end": v(12.4, -10.11) * mm});
            skLineSegment(sketch, "E291", {"start": v(12.4, -10.11) * mm, "end": v(12.4, -10.2) * mm});
            skLineSegment(sketch, "E292", {"start": v(12.4, -10.2) * mm, "end": v(12.4, -10.27) * mm});
            skLineSegment(sketch, "E293", {"start": v(12.4, -10.27) * mm, "end": v(12.3, -10.46) * mm});
            skLineSegment(sketch, "E294", {"start": v(12.3, -10.46) * mm, "end": v(12.28, -10.48) * mm});
            skLineSegment(sketch, "E295", {"start": v(12.28, -10.48) * mm, "end": v(12.27, -10.5) * mm});
            skLineSegment(sketch, "E296", {"start": v(12.27, -10.5) * mm, "end": v(12.08, -10.6) * mm});
            skLineSegment(sketch, "E297", {"start": v(12.08, -10.6) * mm, "end": v(12.02, -10.6) * mm});
            skLineSegment(sketch, "E298", {"start": v(12.02, -10.6) * mm, "end": v(12, -10.6) * mm});
            skLineSegment(sketch, "E299", {"start": v(12, -10.6) * mm, "end": v(11.9, -10.65) * mm});
            skLineSegment(sketch, "E300", {"start": v(11.9, -10.65) * mm, "end": v(11.9, -10.67) * mm});
            skLineSegment(sketch, "E301", {"start": v(11.9, -10.67) * mm, "end": v(11.9, -10.8) * mm});
            skLineSegment(sketch, "E302", {"start": v(11.9, -10.8) * mm, "end": v(12.32, -11.2) * mm});
            skLineSegment(sketch, "E303", {"start": v(12.32, -11.2) * mm, "end": v(12.4, -11.24) * mm});
            skLineSegment(sketch, "E304", {"start": v(12.4, -11.24) * mm, "end": v(12.5, -11.28) * mm});
            skLineSegment(sketch, "E305", {"start": v(12.5, -11.28) * mm, "end": v(13.27, -11.49) * mm});
            skLineSegment(sketch, "E306", {"start": v(13.27, -11.49) * mm, "end": v(13.53, -11.49) * mm});
            skLineSegment(sketch, "E307", {"start": v(13.53, -11.49) * mm, "end": v(13.7, -11.49) * mm});
            skLineSegment(sketch, "E308", {"start": v(13.7, -11.49) * mm, "end": v(14.22, -11.37) * mm});
            skLineSegment(sketch, "E309", {"start": v(14.22, -11.37) * mm, "end": v(14.7, -11.1) * mm});
            skLineSegment(sketch, "E310", {"start": v(14.7, -11.1) * mm, "end": v(14.78, -11.02) * mm});
            skLineSegment(sketch, "E311", {"start": v(14.78, -11.02) * mm, "end": v(14.86, -10.94) * mm});
            skLineSegment(sketch, "E312", {"start": v(14.86, -10.94) * mm, "end": v(15.15, -10.48) * mm});
            skLineSegment(sketch, "E313", {"start": v(15.15, -10.48) * mm, "end": v(15.27, -9.98) * mm});
            skLineSegment(sketch, "E314", {"start": v(15.27, -9.98) * mm, "end": v(15.27, -9.81) * mm});
            skLineSegment(sketch, "E315", {"start": v(15.27, -9.81) * mm, "end": v(15.27, -9.65) * mm});
            skLineSegment(sketch, "E316", {"start": v(15.27, -9.65) * mm, "end": v(15.17, -9.18) * mm});
            skLineSegment(sketch, "E317", {"start": v(15.17, -9.18) * mm, "end": v(14.93, -8.77) * mm});
            skLineSegment(sketch, "E318", {"start": v(14.93, -8.77) * mm, "end": v(14.86, -8.7) * mm});
            skLineSegment(sketch, "E319", {"start": v(14.86, -8.7) * mm, "end": v(14.79, -8.63) * mm});
            skLineSegment(sketch, "E320", {"start": v(14.79, -8.63) * mm, "end": v(14.36, -8.4) * mm});
            skLineSegment(sketch, "E321", {"start": v(14.36, -8.4) * mm, "end": v(13.88, -8.3) * mm});
            skLineSegment(sketch, "E322", {"start": v(13.88, -8.3) * mm, "end": v(13.72, -8.3) * mm});
            skLineSegment(sketch, "E323", {"start": v(13.72, -8.3) * mm, "end": v(13.52, -8.3) * mm});
            skLineSegment(sketch, "E324", {"start": v(13.52, -8.3) * mm, "end": v(12.92, -8.43) * mm});
            skLineSegment(sketch, "E325", {"start": v(12.92, -8.43) * mm, "end": v(12.4, -8.72) * mm});
            skLineSegment(sketch, "E326", {"start": v(12.4, -8.72) * mm, "end": v(12.3, -8.81) * mm});
            skLineSegment(sketch, "E327", {"start": v(12.3, -8.81) * mm, "end": v(12.27, -8.84) * mm});
            skLineSegment(sketch, "E328", {"start": v(12.27, -8.84) * mm, "end": v(12.03, -9.06) * mm});
            skLineSegment(sketch, "E329", {"start": v(12.03, -9.06) * mm, "end": v(12.01, -9.07) * mm});
            skLineSegment(sketch, "E330", {"start": v(12.01, -9.07) * mm, "end": v(12, -9.08) * mm});
            skLineSegment(sketch, "E331", {"start": v(12, -9.08) * mm, "end": v(11.82, -9.15) * mm});
            skLineSegment(sketch, "E332", {"start": v(11.82, -9.15) * mm, "end": v(11.8, -9.15) * mm});
            skLineSegment(sketch, "E333", {"start": v(11.8, -9.15) * mm, "end": v(11.76, -9.15) * mm});
            skLineSegment(sketch, "E334", {"start": v(11.76, -9.15) * mm, "end": v(11.69, -9.15) * mm});
            skLineSegment(sketch, "E335", {"start": v(11.69, -9.15) * mm, "end": v(11.48, -9.05) * mm});
            skLineSegment(sketch, "E336", {"start": v(11.48, -9.05) * mm, "end": v(11.39, -8.81) * mm});
            skLineSegment(sketch, "E337", {"start": v(11.39, -8.81) * mm, "end": v(11.39, -8.74) * mm});
            skLineSegment(sketch, "E338", {"start": v(11.39, -8.74) * mm, "end": v(11.39, -8.73) * mm});
            skLineSegment(sketch, "E339", {"start": v(11.39, -8.73) * mm, "end": v(11.4, -8.7) * mm});
            skLineSegment(sketch, "E340", {"start": v(11.4, -8.7) * mm, "end": v(11.4, -8.7) * mm});
            skLineSegment(sketch, "E341", {"start": v(11.4, -8.7) * mm, "end": v(11.53, -6.86) * mm});
            skLineSegment(sketch, "E342", {"start": v(11.53, -6.86) * mm, "end": v(11.53, -6.83) * mm});
            skLineSegment(sketch, "E343", {"start": v(11.53, -6.83) * mm, "end": v(11.54, -6.4) * mm});
            skLineSegment(sketch, "E344", {"start": v(11.54, -6.4) * mm, "end": v(11.55, -6.34) * mm});
            skLineSegment(sketch, "E345", {"start": v(11.55, -6.34) * mm, "end": v(11.55, -6.25) * mm});
            skLineSegment(sketch, "E346", {"start": v(11.55, -6.25) * mm, "end": v(11.61, -5.71) * mm});
            skLineSegment(sketch, "E347", {"start": v(11.61, -5.71) * mm, "end": v(11.62, -5.7) * mm});
            skLineSegment(sketch, "E348", {"start": v(11.62, -5.7) * mm, "end": v(11.63, -5.67) * mm});
            skLineSegment(sketch, "E349", {"start": v(11.63, -5.67) * mm, "end": v(11.89, -5.57) * mm});
            skLineSegment(sketch, "E350", {"start": v(11.89, -5.57) * mm, "end": v(11.97, -5.57) * mm});
            skLineSegment(sketch, "E351", {"start": v(11.97, -5.57) * mm, "end": v(12.02, -5.57) * mm});
            skLineSegment(sketch, "E352", {"start": v(12.02, -5.57) * mm, "end": v(12.14, -5.58) * mm});
            skLineSegment(sketch, "E353", {"start": v(12.14, -5.58) * mm, "end": v(12.15, -5.58) * mm});
            skLineSegment(sketch, "E354", {"start": v(12.15, -5.58) * mm, "end": v(12.61, -5.57) * mm});
            skLineSegment(sketch, "E355", {"start": v(12.61, -5.57) * mm, "end": v(14.34, -5.57) * mm});
            skLineSegment(sketch, "E356", {"start": v(14.34, -5.57) * mm, "end": v(14.44, -5.57) * mm});
            skLineSegment(sketch, "E357", {"start": v(14.44, -5.57) * mm, "end": v(14.73, -5.56) * mm});
            skLineSegment(sketch, "E358", {"start": v(14.73, -5.56) * mm, "end": v(14.76, -5.56) * mm});
            skLineSegment(sketch, "E359", {"start": v(14.76, -5.56) * mm, "end": v(14.8, -5.56) * mm});
            skLineSegment(sketch, "E360", {"start": v(14.8, -5.56) * mm, "end": v(15.06, -5.54) * mm});
            skLineSegment(sketch, "E361", {"start": v(15.06, -5.54) * mm, "end": v(15.15, -5.54) * mm});
            skLineSegment(sketch, "E362", {"start": v(15.15, -5.54) * mm, "end": v(15.22, -5.54) * mm});
            skLineSegment(sketch, "E363", {"start": v(15.22, -5.54) * mm, "end": v(15.43, -5.68) * mm});
            skLineSegment(sketch, "E364", {"start": v(15.43, -5.68) * mm, "end": v(15.53, -6) * mm});
            skLineSegment(sketch, "E365", {"start": v(15.53, -6) * mm, "end": v(15.53, -6.1) * mm});
            skLineSegment(sketch, "E366", {"start": v(15.53, -6.1) * mm, "end": v(15.52, -6.17) * mm});
            skLineSegment(sketch, "E367", {"start": v(15.52, -6.17) * mm, "end": v(15.52, -6.32) * mm});
            skLineSegment(sketch, "E368", {"start": v(15.52, -6.32) * mm, "end": v(15.58, -6.7) * mm});
            skLineSegment(sketch, "E369", {"start": v(15.58, -6.7) * mm, "end": v(15.6, -6.75) * mm});
            skLineSegment(sketch, "E370", {"start": v(15.6, -6.75) * mm, "end": v(15.6, -6.77) * mm});
            skLineSegment(sketch, "E371", {"start": v(15.6, -6.77) * mm, "end": v(15.63, -6.92) * mm});
            skLineSegment(sketch, "E372", {"start": v(15.63, -6.92) * mm, "end": v(15.63, -6.96) * mm});
            skLineSegment(sketch, "E373", {"start": v(15.63, -6.96) * mm, "end": v(15.63, -7.04) * mm});
            skLineSegment(sketch, "E374", {"start": v(15.63, -7.04) * mm, "end": v(15.39, -7.27) * mm});
            skLineSegment(sketch, "E375", {"start": v(15.39, -7.27) * mm, "end": v(15.3, -7.27) * mm});
            skLineSegment(sketch, "E376", {"start": v(15.3, -7.27) * mm, "end": v(15.25, -7.27) * mm});
            skLineSegment(sketch, "E377", {"start": v(15.25, -7.27) * mm, "end": v(15.08, -7.15) * mm});
            skLineSegment(sketch, "E378", {"start": v(15.08, -7.15) * mm, "end": v(14.99, -6.9) * mm});
            skLineSegment(sketch, "E379", {"start": v(14.99, -6.9) * mm, "end": v(14.98, -6.82) * mm});
            skLineSegment(sketch, "E380", {"start": v(14.98, -6.82) * mm, "end": v(14.98, -6.73) * mm});
            skLineSegment(sketch, "E381", {"start": v(14.98, -6.73) * mm, "end": v(14.86, -6.42) * mm});
            skLineSegment(sketch, "E382", {"start": v(14.86, -6.42) * mm, "end": v(14.6, -6.29) * mm});
            skLineSegment(sketch, "E383", {"start": v(14.6, -6.29) * mm, "end": v(14.52, -6.29) * mm});
            skLineSegment(sketch, "E384", {"start": v(14.52, -6.29) * mm, "end": v(12.53, -6.29) * mm});
            skLineSegment(sketch, "E385", {"start": v(12.53, -6.29) * mm, "end": v(12.46, -6.29) * mm});
            skLineSegment(sketch, "E386", {"start": v(12.46, -6.29) * mm, "end": v(12.27, -6.57) * mm});
            skLineSegment(sketch, "E387", {"start": v(12.27, -6.57) * mm, "end": v(12.26, -6.63) * mm});
            skSolve(sketch);
        }
        {
            var Q0;
            Q0 = qSketchRegion(id + "F3", true);
            var Q1;
            Q1 = qSketchRegion(id + "F4", true);
            extrude(context, id + "F5", {"entities" : qUnion([Q0, Q1]), "depth" : -3 * mm});
        }
    });
